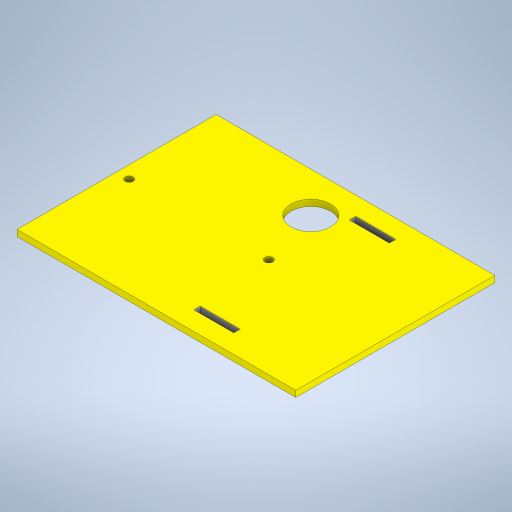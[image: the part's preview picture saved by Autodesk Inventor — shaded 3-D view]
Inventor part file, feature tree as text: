
AUTODESK INVENTOR PART (.ipt)
format: ipt  version: 2024 (Build 280153000, 153)  size: 321,536 bytes
history: native  units: mm
features: sketch x6, extrude x5
ambient origin geometry x8: Origin, YZ Plane, XZ Plane, XY Plane, X Axis, Y Axis, Z Axis, Center Point
bodies: Solid1 (feature_tree)
feature tree (11):
  extrude  "Extrusion1"  Depth=100.0mm
  extrude  "Extrusion9"  Depth=20.0mm
  extrude  "Extrusion10"  Depth=10.0mm
  extrude  "Extrusion11"  Depth=4.0mm
  sketch  "Sketch12"  dims[d48=5.0mm d49=0.0mm d60=20.0mm]
  extrude  "Extrusion13"  Depth=20.0mm
  sketch  "Sketch1"  dims[d0=140.0mm d1=100.0mm]
  sketch  "Sketch9"  dims[d2=3.125mm d3=0.0mm d41=20.0mm]
  sketch  "Sketch10"  dims[d42=10.0mm d43=0.0mm d44=4.0mm]
  sketch  "Sketch11"  dims[d45=5.0mm d46=0.0mm d47=4.0mm]
  sketch  "Sketch14"  dims[d61=3.155mm d62=20.0mm d63=3.155mm d64=75.0mm d65=3.125mm d66=0.0mm d67=9.3mm]
